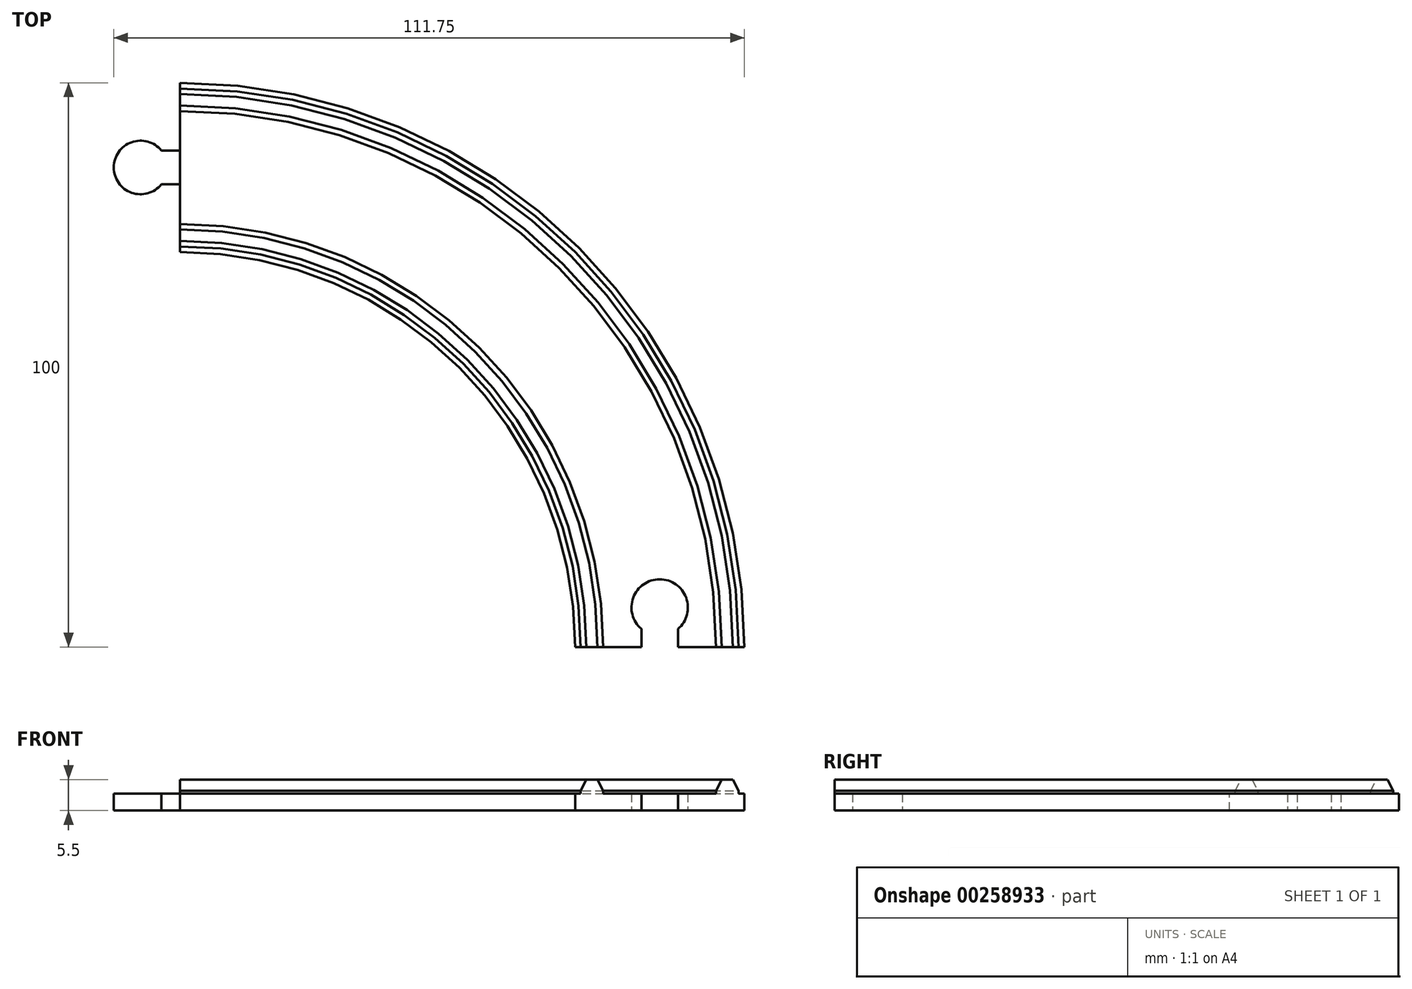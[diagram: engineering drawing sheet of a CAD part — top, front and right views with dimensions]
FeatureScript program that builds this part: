
annotation { "Feature Type Name" : "Feature", "Feature Type Description" : "" }
export const myFeature = defineFeature(function(context is Context, id is Id, definition is map)
    precondition{}
    {
        {
            var Q0;
            Q0=qCreatedBy(makeId("Front.planeOp"),FACE);
            var sketch = newSketch(context, id + "F0", { "sketchPlane" : qUnion([Q0])});
            skLineSegment(sketch, "E0.bottom", {"start": v(52.52, 14.1) * mm, "end": v(82.52, 14.1) * mm});
            skLineSegment(sketch, "E0.top", {"start": v(52.52, 17.1) * mm, "end": v(82.52, 17.1) * mm});
            skLineSegment(sketch, "E0.left", {"start": v(52.52, 14.1) * mm, "end": v(52.52, 17.1) * mm});
            skLineSegment(sketch, "E0.right", {"start": v(82.52, 14.1) * mm, "end": v(82.52, 17.1) * mm});
            skLineSegment(sketch, "E1", {"start": v(53.52, 17.1) * mm, "end": v(53.52, 17.6) * mm});
            skLineSegment(sketch, "E2", {"start": v(53.52, 17.6) * mm, "end": v(54.52, 19.6) * mm});
            skLineSegment(sketch, "E3", {"start": v(54.52, 19.6) * mm, "end": v(56.52, 19.6) * mm});
            skLineSegment(sketch, "E4", {"start": v(56.52, 19.6) * mm, "end": v(57.52, 17.6) * mm});
            skLineSegment(sketch, "E5", {"start": v(57.52, 17.6) * mm, "end": v(57.52, 17.1) * mm});
            skLineSegment(sketch, "E6", {"start": v(77.52, 17.1) * mm, "end": v(77.52, 17.6) * mm});
            skLineSegment(sketch, "E7", {"start": v(77.52, 17.6) * mm, "end": v(78.52, 19.6) * mm});
            skLineSegment(sketch, "E8", {"start": v(78.52, 19.6) * mm, "end": v(80.52, 19.6) * mm});
            skLineSegment(sketch, "E9", {"start": v(80.52, 19.6) * mm, "end": v(81.52, 17.6) * mm});
            skLineSegment(sketch, "E10", {"start": v(81.52, 17.6) * mm, "end": v(81.52, 17.1) * mm});
            skLineSegment(sketch, "E11", {"start": v(-17.48, 14.1) * mm, "end": v(-17.48, 19.1) * mm});
            skSolve(sketch);
        }
        {
            var Q0;
            Q0=makeQuery(id+"F0.imprint","IMPRINT",FACE,{"disambiguationData":[TD([[makeQuery(id+"F0.imprint","IMPRINT",EDGE,{"derivedFrom":sQuery(id+"F0.wireOp",EDGE,"E0.bottom")}),1.0]])]});
            var Q1;
            {var subQ0=sQuery(id+"F0.wireOp",EDGE,"E6");Q1=makeQuery(id+"F0.imprint","IMPRINT",FACE,{"disambiguationData":[TD([[makeQuery(id+"F0.imprint","IMPRINT",EDGE,{"derivedFrom":subQ0}),-1.0]])]});}
            var Q2;
            {var subQ0=sQuery(id+"F0.wireOp",EDGE,"E1");Q2=makeQuery(id+"F0.imprint","IMPRINT",FACE,{"disambiguationData":[TD([[makeQuery(id+"F0.imprint","IMPRINT",EDGE,{"derivedFrom":subQ0}),-1.0]])]});}
            var Q3;
            Q3=sQuery(id+"F0.wireOp",EDGE,"E11");
            revolve(context, id + "F1", {"entities" : qUnion([Q0, Q1, Q2]), "axis" : qUnion([Q3]), "revolveType" : RevolveType.ONE_DIRECTION, "angle" : 90 * degree});
        }
        {
            var Q0;
            Q0=makeQuery(id+"F1.opRevolve","SWEPT_FACE",FACE,{"disambiguationData":[OSD([sQuery(id+"F0.wireOp",EDGE,"E0.bottom")])]});
            var sketch = newSketch(context, id + "F2", { "sketchPlane" : qUnion([Q0])});
            skLineSegment(sketch, "E12", {"start": v(67.52, 0) * mm, "end": v(67.52, -7) * mm});
            skCircle(sketch, "E13", {"center": v(67.52, -7) * mm, "radius": 5 * mm});
            skLineSegment(sketch, "E14", {"start": v(70.77, 0) * mm, "end": v(70.77, -3.2) * mm});
            skLineSegment(sketch, "E15", {"start": v(64.27, 0) * mm, "end": v(64.27, -3.2) * mm});
            skSolve(sketch);
        }
        {
            var Q0;
            {var subQ0=sQuery(id+"F2.wireOp",EDGE,"E13");var subQ1=makeQuery(id+"F2.imprint","INTERSECT",VERTEX,{"derivedFrom":[subQ0,sQuery(id+"F2.wireOp",EDGE,"E14")]});Q0=makeQuery(id+"F2.imprint","IMPRINT",FACE,{"disambiguationData":[TD([[makeQuery(id+"F2.imprint","IMPRINT",EDGE,{"disambiguationData":[TD([[subQ1,-1.0]])],"derivedFrom":subQ0}),1.0]])]});}
            var Q1;
            {var subQ5=sQuery(id+"F2.wireOp",EDGE,"E15");Q1=makeQuery(id+"F2.imprint","IMPRINT",FACE,{"disambiguationData":[TD([[makeQuery(id+"F2.imprint","IMPRINT",EDGE,{"derivedFrom":subQ5}),1.0]])]});}
            var Q2;
            {var subQ5=sQuery(id+"F2.wireOp",EDGE,"E14");Q2=makeQuery(id+"F2.imprint","IMPRINT",FACE,{"disambiguationData":[TD([[makeQuery(id+"F2.imprint","IMPRINT",EDGE,{"derivedFrom":subQ5}),-1.0]])]});}
            extrude(context, id + "F3", {"entities" : qUnion([Q0, Q1, Q2]), "operationType" : NewBodyOperationType.REMOVE, "oppositeDirection" : true, "depth" : 25 * mm});
        }
        {
            var Q0;
            Q0=makeQuery(id+"F1.opRevolve","SWEPT_FACE",FACE,{"disambiguationData":[OSD([sQuery(id+"F0.wireOp",EDGE,"E0.bottom")])]});
            var sketch = newSketch(context, id + "F4", { "sketchPlane" : qUnion([Q0])});
            skLineSegment(sketch, "E16", {"start": v(-17.48, -85) * mm, "end": v(-24.48, -85) * mm});
            skCircle(sketch, "E17", {"center": v(-24.48, -85) * mm, "radius": 4.75 * mm});
            skLineSegment(sketch, "E18", {"start": v(-17.48, -88) * mm, "end": v(-20.8, -88) * mm});
            skLineSegment(sketch, "E19", {"start": v(-17.48, -82) * mm, "end": v(-20.8, -82) * mm});
            skSolve(sketch);
        }
        {
            var Q0;
            {var subQ5=sQuery(id+"F4.wireOp",EDGE,"E18");Q0=makeQuery(id+"F4.imprint","IMPRINT",FACE,{"disambiguationData":[TD([[makeQuery(id+"F4.imprint","IMPRINT",EDGE,{"derivedFrom":subQ5}),-1.0]])]});}
            var Q1;
            {var subQ5=sQuery(id+"F4.wireOp",EDGE,"E19");Q1=makeQuery(id+"F4.imprint","IMPRINT",FACE,{"disambiguationData":[TD([[makeQuery(id+"F4.imprint","IMPRINT",EDGE,{"derivedFrom":subQ5}),1.0]])]});}
            var Q2;
            {var subQ0=sQuery(id+"F4.wireOp",EDGE,"E17");var subQ1=makeQuery(id+"F4.imprint","INTERSECT",VERTEX,{"derivedFrom":[subQ0,sQuery(id+"F4.wireOp",EDGE,"E19")]});Q2=makeQuery(id+"F4.imprint","IMPRINT",FACE,{"disambiguationData":[TD([[makeQuery(id+"F4.imprint","IMPRINT",EDGE,{"disambiguationData":[TD([[subQ1,1.0]])],"derivedFrom":subQ0}),1.0]])]});}
            extrude(context, id + "F5", {"entities" : qUnion([Q0, Q1, Q2]), "oppositeDirection" : true, "depth" : 3 * mm});
        }
    });
